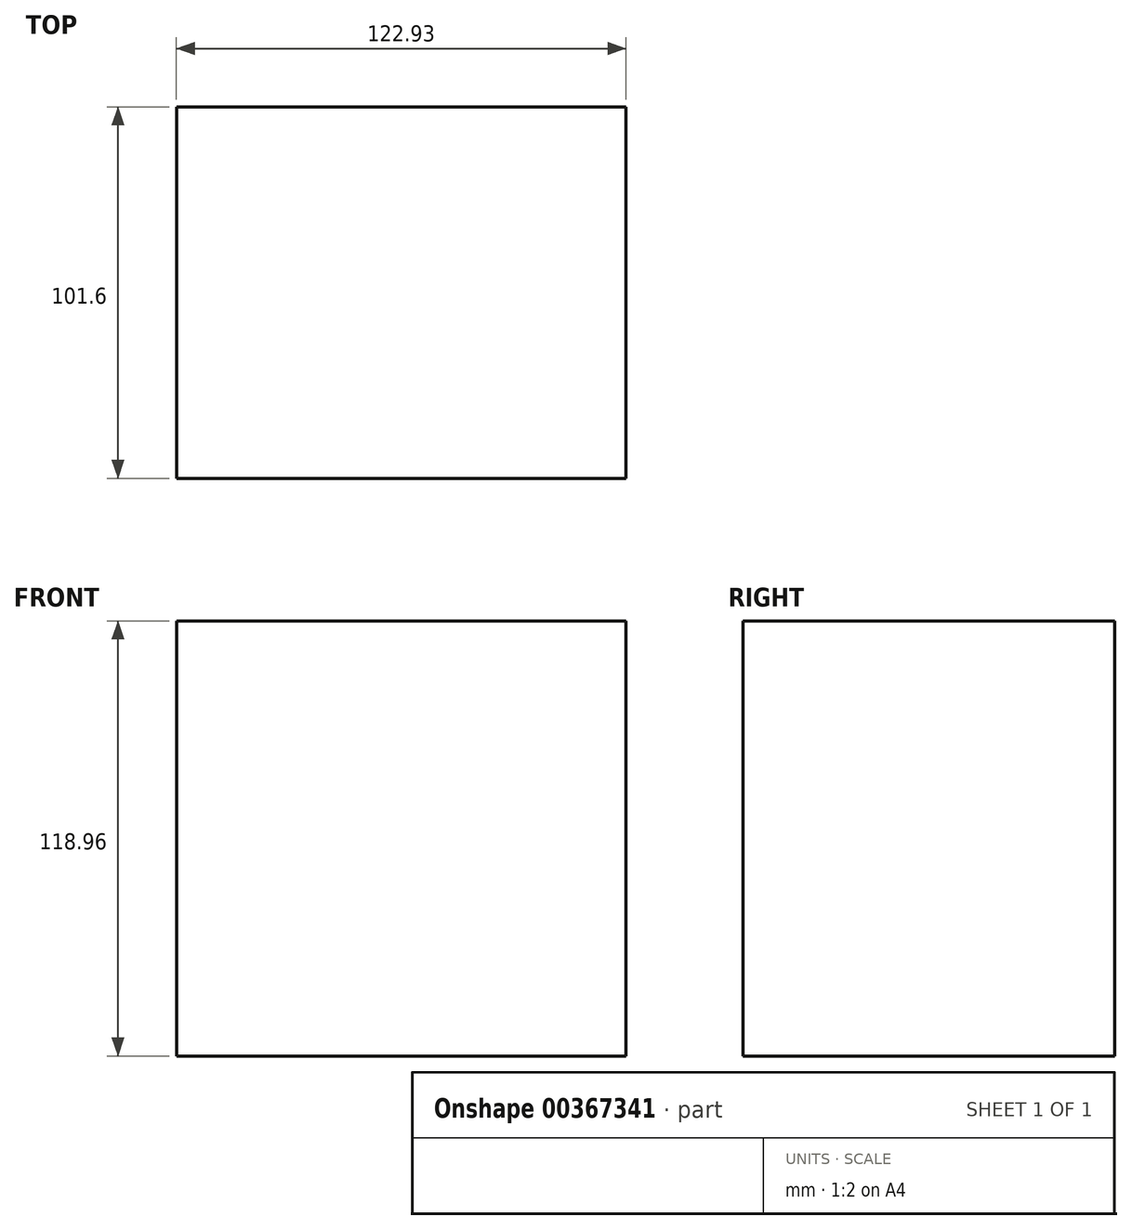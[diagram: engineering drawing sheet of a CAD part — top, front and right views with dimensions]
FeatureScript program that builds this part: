
annotation { "Feature Type Name" : "Feature", "Feature Type Description" : "" }
export const myFeature = defineFeature(function(context is Context, id is Id, definition is map)
    precondition{}
    {
        {
            var Q0;
            Q0=qCreatedBy(makeId("Front.planeOp"),FACE);
            var sketch = newSketch(context, id + "F0", { "sketchPlane" : qUnion([Q0])});
            skLineSegment(sketch, "E0.bottom", {"start": v(-58.62, -52.64) * mm, "end": v(64.3, -52.64) * mm});
            skLineSegment(sketch, "E0.top", {"start": v(-58.62, 66.32) * mm, "end": v(64.3, 66.32) * mm});
            skLineSegment(sketch, "E0.left", {"start": v(-58.62, -52.64) * mm, "end": v(-58.62, 66.32) * mm});
            skLineSegment(sketch, "E0.right", {"start": v(64.3, -52.64) * mm, "end": v(64.3, 66.32) * mm});
            skSolve(sketch);
        }
        {
            var Q0;
            Q0 = qSketchRegion(id + "F0", true);
            extrude(context, id + "F1", {"entities" : qUnion([Q0]), "depth" : 101.6 * mm});
        }
    });
